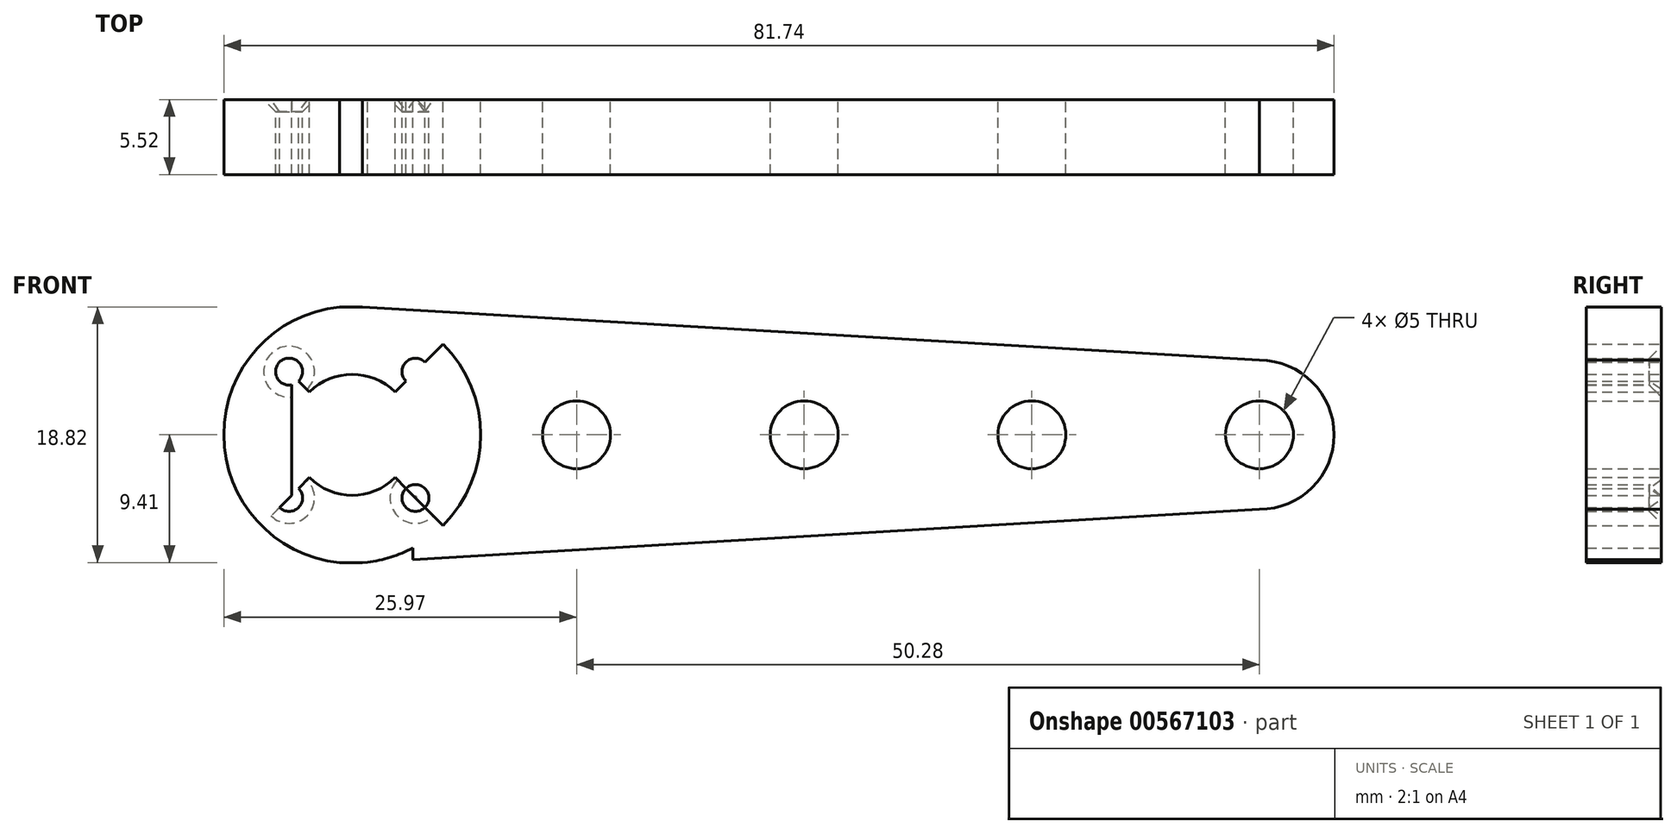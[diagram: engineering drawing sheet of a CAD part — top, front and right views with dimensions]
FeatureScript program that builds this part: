
annotation { "Feature Type Name" : "Feature", "Feature Type Description" : "" }
export const myFeature = defineFeature(function(context is Context, id is Id, definition is map)
    precondition{}
    {
        {
            var Q0;
            Q0=qCreatedBy(makeId("Front.planeOp"),FACE);
            var sketch = newSketch(context, id + "F0", { "sketchPlane" : qUnion([Q0])});
            skLineSegment(sketch, "E0.bottom", {"start": v(40.87, 9.41) * mm, "end": v(-40.87, 9.41) * mm});
            skLineSegment(sketch, "E0.top", {"start": v(40.87, -9.4) * mm, "end": v(-40.87, -9.4) * mm});
            skLineSegment(sketch, "E0.left", {"start": v(40.87, 9.41) * mm, "end": v(40.87, -9.4) * mm});
            skLineSegment(sketch, "E0.right", {"start": v(-40.87, 9.41) * mm, "end": v(-40.87, -9.4) * mm});
            skPoint(sketch, "E0.middle", {"position": v(0, 0) * mm});
            skLineSegment(sketch, "E1", {"start": v(-35.87, 9.41) * mm, "end": v(-35.87, -9.4) * mm});
            skLineSegment(sketch, "E2", {"start": v(-26.96, 9.41) * mm, "end": v(-26.96, -9.4) * mm});
            skLineSegment(sketch, "E3", {"start": v(-35.87, 0) * mm, "end": v(-26.96, 0) * mm});
            skCircle(sketch, "E4", {"center": v(-31.41, 0) * mm, "radius": 4.46 * mm});
            skLineSegment(sketch, "E5", {"start": v(32.88, 9.4) * mm, "end": v(32.88, -9.4) * mm});
            skLineSegment(sketch, "E6", {"start": v(37.88, 9.4) * mm, "end": v(37.88, -9.4) * mm});
            skLineSegment(sketch, "E7", {"start": v(37.88, 0) * mm, "end": v(32.88, 0) * mm});
            skCircle(sketch, "E8", {"center": v(35.38, 0) * mm, "radius": 2.5 * mm});
            skLineSegment(sketch, "E9", {"start": v(21.12, 9.4) * mm, "end": v(21.12, -9.4) * mm});
            skLineSegment(sketch, "E10", {"start": v(16.12, 9.4) * mm, "end": v(16.12, -9.4) * mm});
            skLineSegment(sketch, "E11", {"start": v(4.36, 9.4) * mm, "end": v(4.36, -9.4) * mm});
            skLineSegment(sketch, "E12", {"start": v(-0.64, 9.4) * mm, "end": v(-0.64, -9.4) * mm});
            skLineSegment(sketch, "E13", {"start": v(-12.4, 9.4) * mm, "end": v(-12.4, -9.4) * mm});
            skLineSegment(sketch, "E14", {"start": v(-17.4, 9.4) * mm, "end": v(-17.4, -9.4) * mm});
            skLineSegment(sketch, "E15", {"start": v(-17.4, 0) * mm, "end": v(-12.4, 0) * mm});
            skLineSegment(sketch, "E16", {"start": v(-0.64, 0) * mm, "end": v(4.36, 0) * mm});
            skLineSegment(sketch, "E17", {"start": v(16.12, 0) * mm, "end": v(21.12, 0) * mm});
            skCircle(sketch, "E18", {"center": v(-14.9, 0) * mm, "radius": 2.5 * mm});
            skCircle(sketch, "E19", {"center": v(1.86, 0) * mm, "radius": 2.5 * mm});
            skCircle(sketch, "E20", {"center": v(18.62, 0) * mm, "radius": 2.5 * mm});
            skLineSegment(sketch, "E21", {"start": v(-31.41, 0) * mm, "end": v(-40.67, 9.25) * mm});
            skLineSegment(sketch, "E22", {"start": v(-31.41, 0) * mm, "end": v(-22.16, 9.25) * mm});
            skLineSegment(sketch, "E23", {"start": v(-31.41, 0) * mm, "end": v(-22.16, -9.25) * mm});
            skLineSegment(sketch, "E24", {"start": v(-31.41, 0) * mm, "end": v(-40.67, -9.25) * mm});
            skLineSegment(sketch, "E25", {"start": v(-28.26, 3.15) * mm, "end": v(-28.26, -3.15) * mm});
            skLineSegment(sketch, "E26", {"start": v(-28.26, -3.15) * mm, "end": v(-34.57, -3.15) * mm});
            skLineSegment(sketch, "E27", {"start": v(-34.57, -3.15) * mm, "end": v(-34.57, 3.15) * mm});
            skLineSegment(sketch, "E28", {"start": v(-34.57, 3.15) * mm, "end": v(-28.26, 3.15) * mm});
            skLineSegment(sketch, "E29", {"start": v(-28.26, 3.15) * mm, "end": v(-27.47, 3.95) * mm});
            skLineSegment(sketch, "E30", {"start": v(-27.47, 3.95) * mm, "end": v(-26.06, 5.35) * mm});
            skCircle(sketch, "E31", {"center": v(-26.76, 4.65) * mm, "radius": 1 * mm});
            skCircle(sketch, "E32.MirrorC", {"center": v(-26.76, -4.65) * mm, "radius": 1 * mm});
            skCircle(sketch, "E33.MirrorC", {"center": v(-36.07, -4.65) * mm, "radius": 1 * mm});
            skCircle(sketch, "E34.MirrorC", {"center": v(-36.07, 4.65) * mm, "radius": 1 * mm});
            skCircle(sketch, "E35", {"center": v(-31.41, 0) * mm, "radius": 9.46 * mm});
            skCircle(sketch, "E36", {"center": v(35.38, 0) * mm, "radius": 5.49 * mm});
            skLineSegment(sketch, "E37", {"start": v(35.38, 0) * mm, "end": v(35.38, 5.49) * mm});
            skLineSegment(sketch, "E38", {"start": v(35.38, 0) * mm, "end": v(35.38, -5.49) * mm});
            skLineSegment(sketch, "E39", {"start": v(-31.41, 0) * mm, "end": v(-31.41, -9.46) * mm});
            skLineSegment(sketch, "E40", {"start": v(-31.41, 0) * mm, "end": v(-31.41, 9.46) * mm});
            skLineSegment(sketch, "E41", {"start": v(-31.41, 9.46) * mm, "end": v(35.38, 5.49) * mm});
            skLineSegment(sketch, "E42", {"start": v(35.38, -5.49) * mm, "end": v(-31.41, -9.46) * mm});
            skSolve(sketch);
        }
        {
            var Q0;
            {var subQ5=sQuery(id+"F0.wireOp",EDGE,"E35");var subQ11=sQuery(id+"F0.wireOp",EDGE,"E0.bottom");var subQ12=makeQuery(id+"F0.imprint","INTERSECT",VERTEX,{"disambiguationData":[OD(1.0)],"derivedFrom":[subQ11,subQ5]});Q0=makeQuery(id+"F0.imprint","IMPRINT",FACE,{"disambiguationData":[TD([[makeQuery(id+"F0.imprint","IMPRINT",EDGE,{"disambiguationData":[TD([[subQ12,1.0]])],"derivedFrom":subQ11}),1.0]])]});}
            var Q1;
            {var subQ0=sQuery(id+"F0.wireOp",EDGE,"E35");var subQ5=sQuery(id+"F0.wireOp",EDGE,"E21");var subQ6=makeQuery(id+"F0.imprint","INTERSECT",VERTEX,{"derivedFrom":[subQ5,subQ0]});Q1=makeQuery(id+"F0.imprint","IMPRINT",FACE,{"disambiguationData":[TD([[makeQuery(id+"F0.imprint","IMPRINT",EDGE,{"disambiguationData":[TD([[subQ6,1.0]])],"derivedFrom":subQ5}),1.0]])]});}
            var Q2;
            {var subQ0=sQuery(id+"F0.wireOp",EDGE,"E35");var subQ1=sQuery(id+"F0.wireOp",EDGE,"E1");var subQ2=makeQuery(id+"F0.imprint","INTERSECT",VERTEX,{"disambiguationData":[OD(0.0)],"derivedFrom":[subQ1,subQ0]});Q2=makeQuery(id+"F0.imprint","IMPRINT",FACE,{"disambiguationData":[TD([[makeQuery(id+"F0.imprint","IMPRINT",EDGE,{"disambiguationData":[TD([[subQ2,-1.0]])],"derivedFrom":subQ1}),-1.0]])]});}
            var Q3;
            {var subQ1=sQuery(id+"F0.wireOp",EDGE,"E1");var subQ3=sQuery(id+"F0.wireOp",EDGE,"E34.MirrorC");var subQ4=makeQuery(id+"F0.imprint","INTERSECT",VERTEX,{"disambiguationData":[OD(1.0)],"derivedFrom":[subQ1,subQ3]});Q3=makeQuery(id+"F0.imprint","IMPRINT",FACE,{"disambiguationData":[TD([[makeQuery(id+"F0.imprint","IMPRINT",EDGE,{"disambiguationData":[TD([[subQ4,-1.0]])],"derivedFrom":subQ3}),-1.0]])]});}
            var Q4;
            {var subQ0=sQuery(id+"F0.wireOp",EDGE,"E33.MirrorC");var subQ1=sQuery(id+"F0.wireOp",EDGE,"E1");var subQ2=makeQuery(id+"F0.imprint","INTERSECT",VERTEX,{"disambiguationData":[OD(1.0)],"derivedFrom":[subQ1,subQ0]});Q4=makeQuery(id+"F0.imprint","IMPRINT",FACE,{"disambiguationData":[TD([[makeQuery(id+"F0.imprint","IMPRINT",EDGE,{"disambiguationData":[TD([[subQ2,-1.0]])],"derivedFrom":subQ1}),-1.0]])]});}
            var Q5;
            {var subQ9=sQuery(id+"F0.wireOp",EDGE,"E35");var subQ11=sQuery(id+"F0.wireOp",EDGE,"E0.top");var subQ12=makeQuery(id+"F0.imprint","INTERSECT",VERTEX,{"disambiguationData":[OD(1.0)],"derivedFrom":[subQ11,subQ9]});Q5=makeQuery(id+"F0.imprint","IMPRINT",FACE,{"disambiguationData":[TD([[makeQuery(id+"F0.imprint","IMPRINT",EDGE,{"disambiguationData":[TD([[subQ12,1.0]])],"derivedFrom":subQ11}),-1.0]])]});}
            var Q6;
            {var subQ1=sQuery(id+"F0.wireOp",EDGE,"E1");var subQ3=sQuery(id+"F0.wireOp",EDGE,"E33.MirrorC");var subQ4=makeQuery(id+"F0.imprint","INTERSECT",VERTEX,{"disambiguationData":[OD(0.0)],"derivedFrom":[subQ1,subQ3]});Q6=makeQuery(id+"F0.imprint","IMPRINT",FACE,{"disambiguationData":[TD([[makeQuery(id+"F0.imprint","IMPRINT",EDGE,{"disambiguationData":[TD([[subQ4,-1.0]])],"derivedFrom":subQ3}),1.0]])]});}
            var Q7;
            {var subQ11=sQuery(id+"F0.wireOp",EDGE,"E42");var subQ12=sQuery(id+"F0.wireOp",EDGE,"E0.top");var subQ13=makeQuery(id+"F0.imprint","INTERSECT",VERTEX,{"derivedFrom":[subQ12,subQ11]});Q7=makeQuery(id+"F0.imprint","IMPRINT",FACE,{"disambiguationData":[TD([[makeQuery(id+"F0.imprint","IMPRINT",EDGE,{"disambiguationData":[TD([[subQ13,-1.0]])],"derivedFrom":subQ12}),-1.0]])]});}
            var Q8;
            {var subQ0=sQuery(id+"F0.wireOp",EDGE,"E32.MirrorC");var subQ1=sQuery(id+"F0.wireOp",EDGE,"E2");var subQ2=makeQuery(id+"F0.imprint","INTERSECT",VERTEX,{"disambiguationData":[OD(1.0)],"derivedFrom":[subQ1,subQ0]});Q8=makeQuery(id+"F0.imprint","IMPRINT",FACE,{"disambiguationData":[TD([[makeQuery(id+"F0.imprint","IMPRINT",EDGE,{"disambiguationData":[TD([[subQ2,-1.0]])],"derivedFrom":subQ1}),1.0]])]});}
            var Q9;
            {var subQ7=sQuery(id+"F0.wireOp",EDGE,"E32.MirrorC");var subQ9=sQuery(id+"F0.wireOp",EDGE,"E23");var subQ10=makeQuery(id+"F0.imprint","INTERSECT",VERTEX,{"disambiguationData":[OD(1.0)],"derivedFrom":[subQ9,subQ7]});Q9=makeQuery(id+"F0.imprint","IMPRINT",FACE,{"disambiguationData":[TD([[makeQuery(id+"F0.imprint","IMPRINT",EDGE,{"disambiguationData":[TD([[subQ10,-1.0]])],"derivedFrom":subQ9}),1.0]])]});}
            var Q10;
            {var subQ1=sQuery(id+"F0.wireOp",EDGE,"E2");var subQ3=sQuery(id+"F0.wireOp",EDGE,"E32.MirrorC");var subQ4=makeQuery(id+"F0.imprint","INTERSECT",VERTEX,{"disambiguationData":[OD(0.0)],"derivedFrom":[subQ1,subQ3]});Q10=makeQuery(id+"F0.imprint","IMPRINT",FACE,{"disambiguationData":[TD([[makeQuery(id+"F0.imprint","IMPRINT",EDGE,{"disambiguationData":[TD([[subQ4,1.0]])],"derivedFrom":subQ3}),1.0]])]});}
            var Q11;
            {var subQ0=sQuery(id+"F0.wireOp",EDGE,"E29");Q11=makeQuery(id+"F0.imprint","IMPRINT",FACE,{"disambiguationData":[TD([[makeQuery(id+"F0.imprint","IMPRINT",EDGE,{"derivedFrom":subQ0}),1.0]])]});}
            var Q12;
            {var subQ0=sQuery(id+"F0.wireOp",EDGE,"E35");var subQ1=sQuery(id+"F0.wireOp",EDGE,"E2");var subQ2=makeQuery(id+"F0.imprint","INTERSECT",VERTEX,{"disambiguationData":[OD(0.0)],"derivedFrom":[subQ1,subQ0]});Q12=makeQuery(id+"F0.imprint","IMPRINT",FACE,{"disambiguationData":[TD([[makeQuery(id+"F0.imprint","IMPRINT",EDGE,{"disambiguationData":[TD([[subQ2,-1.0]])],"derivedFrom":subQ1}),1.0]])]});}
            var Q13;
            {var subQ5=sQuery(id+"F0.wireOp",EDGE,"E29");Q13=makeQuery(id+"F0.imprint","IMPRINT",FACE,{"disambiguationData":[TD([[makeQuery(id+"F0.imprint","IMPRINT",EDGE,{"derivedFrom":subQ5}),-1.0]])]});}
            var Q14;
            {var subQ0=sQuery(id+"F0.wireOp",EDGE,"E41");var subQ1=sQuery(id+"F0.wireOp",EDGE,"E22");var subQ2=makeQuery(id+"F0.imprint","INTERSECT",VERTEX,{"derivedFrom":[subQ1,subQ0]});Q14=makeQuery(id+"F0.imprint","IMPRINT",FACE,{"disambiguationData":[TD([[makeQuery(id+"F0.imprint","IMPRINT",EDGE,{"disambiguationData":[TD([[subQ2,1.0]])],"derivedFrom":subQ1}),-1.0]])]});}
            var Q15;
            {var subQ0=sQuery(id+"F0.wireOp",EDGE,"E41");var subQ1=sQuery(id+"F0.wireOp",EDGE,"E2");var subQ2=makeQuery(id+"F0.imprint","INTERSECT",VERTEX,{"derivedFrom":[subQ1,subQ0]});Q15=makeQuery(id+"F0.imprint","IMPRINT",FACE,{"disambiguationData":[TD([[makeQuery(id+"F0.imprint","IMPRINT",EDGE,{"disambiguationData":[TD([[subQ2,-1.0]])],"derivedFrom":subQ1}),1.0]])]});}
            var Q16;
            {var subQ0=sQuery(id+"F0.wireOp",EDGE,"E41");var subQ1=sQuery(id+"F0.wireOp",EDGE,"E2");var subQ2=makeQuery(id+"F0.imprint","INTERSECT",VERTEX,{"derivedFrom":[subQ1,subQ0]});Q16=makeQuery(id+"F0.imprint","IMPRINT",FACE,{"disambiguationData":[TD([[makeQuery(id+"F0.imprint","IMPRINT",EDGE,{"disambiguationData":[TD([[subQ2,-1.0]])],"derivedFrom":subQ1}),-1.0]])]});}
            var Q17;
            {var subQ0=sQuery(id+"F0.wireOp",EDGE,"E35");var subQ1=sQuery(id+"F0.wireOp",EDGE,"E2");var subQ2=makeQuery(id+"F0.imprint","INTERSECT",VERTEX,{"disambiguationData":[OD(1.0)],"derivedFrom":[subQ1,subQ0]});Q17=makeQuery(id+"F0.imprint","IMPRINT",FACE,{"disambiguationData":[TD([[makeQuery(id+"F0.imprint","IMPRINT",EDGE,{"disambiguationData":[TD([[subQ2,-1.0]])],"derivedFrom":subQ1}),1.0]])]});}
            var Q18;
            {var subQ0=sQuery(id+"F0.wireOp",EDGE,"E35");var subQ1=sQuery(id+"F0.wireOp",EDGE,"E2");var subQ2=makeQuery(id+"F0.imprint","INTERSECT",VERTEX,{"disambiguationData":[OD(1.0)],"derivedFrom":[subQ1,subQ0]});Q18=makeQuery(id+"F0.imprint","IMPRINT",FACE,{"disambiguationData":[TD([[makeQuery(id+"F0.imprint","IMPRINT",EDGE,{"disambiguationData":[TD([[subQ2,-1.0]])],"derivedFrom":subQ1}),-1.0]])]});}
            var Q19;
            {var subQ2=sQuery(id+"F0.wireOp",EDGE,"E13");var subQ4=sQuery(id+"F0.wireOp",EDGE,"E42");var subQ5=makeQuery(id+"F0.imprint","INTERSECT",VERTEX,{"derivedFrom":[subQ2,subQ4]});Q19=makeQuery(id+"F0.imprint","IMPRINT",FACE,{"disambiguationData":[TD([[makeQuery(id+"F0.imprint","IMPRINT",EDGE,{"disambiguationData":[TD([[subQ5,-1.0]])],"derivedFrom":subQ4}),-1.0]])]});}
            var Q20;
            {var subQ2=sQuery(id+"F0.wireOp",EDGE,"E13");var subQ4=sQuery(id+"F0.wireOp",EDGE,"E41");var subQ5=makeQuery(id+"F0.imprint","INTERSECT",VERTEX,{"derivedFrom":[subQ2,subQ4]});Q20=makeQuery(id+"F0.imprint","IMPRINT",FACE,{"disambiguationData":[TD([[makeQuery(id+"F0.imprint","IMPRINT",EDGE,{"disambiguationData":[TD([[subQ5,1.0]])],"derivedFrom":subQ4}),-1.0]])]});}
            var Q21;
            {var subQ2=sQuery(id+"F0.wireOp",EDGE,"E41");var subQ4=sQuery(id+"F0.wireOp",EDGE,"E12");var subQ9=makeQuery(id+"F0.imprint","INTERSECT",VERTEX,{"derivedFrom":[subQ4,subQ2]});Q21=makeQuery(id+"F0.imprint","IMPRINT",FACE,{"disambiguationData":[TD([[makeQuery(id+"F0.imprint","IMPRINT",EDGE,{"disambiguationData":[TD([[subQ9,1.0]])],"derivedFrom":subQ2}),-1.0]])]});}
            var Q22;
            {var subQ2=sQuery(id+"F0.wireOp",EDGE,"E41");var subQ5=sQuery(id+"F0.wireOp",EDGE,"E10");var subQ9=makeQuery(id+"F0.imprint","INTERSECT",VERTEX,{"derivedFrom":[subQ5,subQ2]});Q22=makeQuery(id+"F0.imprint","IMPRINT",FACE,{"disambiguationData":[TD([[makeQuery(id+"F0.imprint","IMPRINT",EDGE,{"disambiguationData":[TD([[subQ9,1.0]])],"derivedFrom":subQ2}),-1.0]])]});}
            var Q23;
            {var subQ2=sQuery(id+"F0.wireOp",EDGE,"E11");var subQ4=sQuery(id+"F0.wireOp",EDGE,"E42");var subQ5=makeQuery(id+"F0.imprint","INTERSECT",VERTEX,{"derivedFrom":[subQ2,subQ4]});Q23=makeQuery(id+"F0.imprint","IMPRINT",FACE,{"disambiguationData":[TD([[makeQuery(id+"F0.imprint","IMPRINT",EDGE,{"disambiguationData":[TD([[subQ5,-1.0]])],"derivedFrom":subQ4}),-1.0]])]});}
            var Q24;
            {var subQ2=sQuery(id+"F0.wireOp",EDGE,"E11");var subQ4=sQuery(id+"F0.wireOp",EDGE,"E41");var subQ5=makeQuery(id+"F0.imprint","INTERSECT",VERTEX,{"derivedFrom":[subQ2,subQ4]});Q24=makeQuery(id+"F0.imprint","IMPRINT",FACE,{"disambiguationData":[TD([[makeQuery(id+"F0.imprint","IMPRINT",EDGE,{"disambiguationData":[TD([[subQ5,1.0]])],"derivedFrom":subQ4}),-1.0]])]});}
            var Q25;
            {var subQ2=sQuery(id+"F0.wireOp",EDGE,"E9");var subQ4=sQuery(id+"F0.wireOp",EDGE,"E41");var subQ5=makeQuery(id+"F0.imprint","INTERSECT",VERTEX,{"derivedFrom":[subQ2,subQ4]});Q25=makeQuery(id+"F0.imprint","IMPRINT",FACE,{"disambiguationData":[TD([[makeQuery(id+"F0.imprint","IMPRINT",EDGE,{"disambiguationData":[TD([[subQ5,1.0]])],"derivedFrom":subQ4}),-1.0]])]});}
            var Q26;
            {var subQ2=sQuery(id+"F0.wireOp",EDGE,"E9");var subQ4=sQuery(id+"F0.wireOp",EDGE,"E42");var subQ5=makeQuery(id+"F0.imprint","INTERSECT",VERTEX,{"derivedFrom":[subQ2,subQ4]});Q26=makeQuery(id+"F0.imprint","IMPRINT",FACE,{"disambiguationData":[TD([[makeQuery(id+"F0.imprint","IMPRINT",EDGE,{"disambiguationData":[TD([[subQ5,-1.0]])],"derivedFrom":subQ4}),-1.0]])]});}
            var Q27;
            {var subQ4=sQuery(id+"F0.wireOp",EDGE,"E41");var subQ7=sQuery(id+"F0.wireOp",EDGE,"E5");var subQ10=makeQuery(id+"F0.imprint","INTERSECT",VERTEX,{"derivedFrom":[subQ7,subQ4]});Q27=makeQuery(id+"F0.imprint","IMPRINT",FACE,{"disambiguationData":[TD([[makeQuery(id+"F0.imprint","IMPRINT",EDGE,{"disambiguationData":[TD([[subQ10,-1.0]])],"derivedFrom":subQ7}),-1.0]])]});}
            var Q28;
            {var subQ0=sQuery(id+"F0.wireOp",EDGE,"E5");var subQ2=sQuery(id+"F0.wireOp",EDGE,"E36");var subQ3=makeQuery(id+"F0.imprint","INTERSECT",VERTEX,{"disambiguationData":[OD(0.0)],"derivedFrom":[subQ0,subQ2]});Q28=makeQuery(id+"F0.imprint","IMPRINT",FACE,{"disambiguationData":[TD([[makeQuery(id+"F0.imprint","IMPRINT",EDGE,{"disambiguationData":[TD([[subQ3,-1.0]])],"derivedFrom":subQ2}),1.0]])]});}
            var Q29;
            {var subQ2=sQuery(id+"F0.wireOp",EDGE,"E36");var subQ4=makeQuery(id+"F0.imprint","INTERSECT",VERTEX,{"derivedFrom":[sQuery(id+"F0.wireOp",EDGE,"E0.left"),subQ2]});Q29=makeQuery(id+"F0.imprint","IMPRINT",FACE,{"disambiguationData":[TD([[makeQuery(id+"F0.imprint","IMPRINT",EDGE,{"disambiguationData":[TD([[subQ4,-1.0]])],"derivedFrom":subQ2}),1.0]])]});}
            var Q30;
            {var subQ1=sQuery(id+"F0.wireOp",EDGE,"E6");var subQ3=sQuery(id+"F0.wireOp",EDGE,"E36");var subQ4=makeQuery(id+"F0.imprint","INTERSECT",VERTEX,{"disambiguationData":[OD(0.0)],"derivedFrom":[subQ1,subQ3]});Q30=makeQuery(id+"F0.imprint","IMPRINT",FACE,{"disambiguationData":[TD([[makeQuery(id+"F0.imprint","IMPRINT",EDGE,{"disambiguationData":[TD([[subQ4,-1.0]])],"derivedFrom":subQ1}),-1.0]])]});}
            var Q31;
            {var subQ1=sQuery(id+"F0.wireOp",EDGE,"E6");var subQ3=sQuery(id+"F0.wireOp",EDGE,"E36");var subQ4=makeQuery(id+"F0.imprint","INTERSECT",VERTEX,{"disambiguationData":[OD(1.0)],"derivedFrom":[subQ1,subQ3]});Q31=makeQuery(id+"F0.imprint","IMPRINT",FACE,{"disambiguationData":[TD([[makeQuery(id+"F0.imprint","IMPRINT",EDGE,{"disambiguationData":[TD([[subQ4,1.0]])],"derivedFrom":subQ1}),-1.0]])]});}
            var Q32;
            {var subQ1=sQuery(id+"F0.wireOp",EDGE,"E5");var subQ3=sQuery(id+"F0.wireOp",EDGE,"E36");var subQ4=makeQuery(id+"F0.imprint","INTERSECT",VERTEX,{"disambiguationData":[OD(1.0)],"derivedFrom":[subQ1,subQ3]});Q32=makeQuery(id+"F0.imprint","IMPRINT",FACE,{"disambiguationData":[TD([[makeQuery(id+"F0.imprint","IMPRINT",EDGE,{"disambiguationData":[TD([[subQ4,1.0]])],"derivedFrom":subQ1}),1.0]])]});}
            var Q33;
            {var subQ1=sQuery(id+"F0.wireOp",EDGE,"E5");var subQ3=sQuery(id+"F0.wireOp",EDGE,"E36");var subQ4=makeQuery(id+"F0.imprint","INTERSECT",VERTEX,{"disambiguationData":[OD(0.0)],"derivedFrom":[subQ1,subQ3]});Q33=makeQuery(id+"F0.imprint","IMPRINT",FACE,{"disambiguationData":[TD([[makeQuery(id+"F0.imprint","IMPRINT",EDGE,{"disambiguationData":[TD([[subQ4,-1.0]])],"derivedFrom":subQ1}),1.0]])]});}
            var Q34;
            {var subQ0=sQuery(id+"F0.wireOp",EDGE,"E36");var subQ1=sQuery(id+"F0.wireOp",EDGE,"E5");var subQ2=makeQuery(id+"F0.imprint","INTERSECT",VERTEX,{"disambiguationData":[OD(1.0)],"derivedFrom":[subQ1,subQ0]});Q34=makeQuery(id+"F0.imprint","IMPRINT",FACE,{"disambiguationData":[TD([[makeQuery(id+"F0.imprint","IMPRINT",EDGE,{"disambiguationData":[TD([[subQ2,-1.0]])],"derivedFrom":subQ1}),1.0]])]});}
            var Q35;
            {var subQ0=sQuery(id+"F0.wireOp",EDGE,"E41");var subQ1=sQuery(id+"F0.wireOp",EDGE,"E5");var subQ2=makeQuery(id+"F0.imprint","INTERSECT",VERTEX,{"derivedFrom":[subQ1,subQ0]});Q35=makeQuery(id+"F0.imprint","IMPRINT",FACE,{"disambiguationData":[TD([[makeQuery(id+"F0.imprint","IMPRINT",EDGE,{"disambiguationData":[TD([[subQ2,-1.0]])],"derivedFrom":subQ1}),1.0]])]});}
            extrude(context, id + "F1", {"entities" : qUnion([Q0, Q1, Q2, Q3, Q4, Q5, Q6, Q7, Q8, Q9, Q10, Q11, Q12, Q13, Q14, Q15, Q16, Q17, Q18, Q19, Q20, Q21, Q22, Q23, Q24, Q25, Q26, Q27, Q28, Q29, Q30, Q31, Q32, Q33, Q34, Q35]), "endBound" : BoundingType.SYMMETRIC, "depth" : 5.52 * mm, "offsetDistance" : 25 * mm});
        }
        {
            var Q0;
            Q0=makeQuery(id+"F1.opExtrude","CAP_EDGE",EDGE,{"disambiguationData":[OSD([sQuery(id+"F0.wireOp",EDGE,"E34.MirrorC")])],"isStart":true});
            var Q1;
            Q1=makeQuery(id+"F1.opExtrude","CAP_EDGE",EDGE,{"disambiguationData":[OSD([sQuery(id+"F0.wireOp",EDGE,"E31")])],"isStart":true});
            var Q2;
            Q2=makeQuery(id+"F1.opExtrude","CAP_EDGE",EDGE,{"disambiguationData":[OSD([sQuery(id+"F0.wireOp",EDGE,"E32.MirrorC")])],"isStart":true});
            var Q3;
            Q3=makeQuery(id+"F1.opExtrude","CAP_EDGE",EDGE,{"disambiguationData":[OSD([sQuery(id+"F0.wireOp",EDGE,"E33.MirrorC")])],"isStart":true});
            chamfer(context, id + "F2", {"entities" : qUnion([Q0, Q1, Q2, Q3]), "chamferType" : ChamferType.OFFSET_ANGLE, "width" : 0.88 * mm, "oppositeDirection" : false, "angle" : 45 * degree});
        }
        {
            var Q0;
            Q0=makeQuery(id+"F1.opExtrude","SWEPT_BODY",BODY,{"disambiguationData":[OSD([sQuery(id+"F0.wireOp",EDGE,"E0.bottom"),sQuery(id+"F0.wireOp",EDGE,"E0.top"),sQuery(id+"F0.wireOp",EDGE,"E4"),sQuery(id+"F0.wireOp",EDGE,"E8"),sQuery(id+"F0.wireOp",EDGE,"E18"),sQuery(id+"F0.wireOp",EDGE,"E19"),sQuery(id+"F0.wireOp",EDGE,"E20"),sQuery(id+"F0.wireOp",EDGE,"E31"),sQuery(id+"F0.wireOp",EDGE,"E32.MirrorC"),sQuery(id+"F0.wireOp",EDGE,"E33.MirrorC"),sQuery(id+"F0.wireOp",EDGE,"E34.MirrorC"),sQuery(id+"F0.wireOp",EDGE,"E35"),sQuery(id+"F0.wireOp",EDGE,"E36"),sQuery(id+"F0.wireOp",EDGE,"E41"),sQuery(id+"F0.wireOp",EDGE,"E42")])]});
            var Q1;
            Q1=makeQuery(id+"F1.opExtrude","CAP_EDGE",EDGE,{"disambiguationData":[OSD([sQuery(id+"F0.wireOp",EDGE,"E41")])],"isStart":false});
            transform(context, id + "F3", {"entities" : qUnion([Q0]), "transformType" : TransformType.ROTATION, "transformAxis" : qUnion([Q1]), "angle" : 180 * degree, "makeCopy" : true});
        }
        {
            var Q0;
            Q0=makeQuery(id+"F3.opPattern","COPY",BODY,{"derivedFrom":makeQuery(id+"F1.opExtrude","SWEPT_BODY",BODY,{"disambiguationData":[OSD([sQuery(id+"F0.wireOp",EDGE,"E0.bottom"),sQuery(id+"F0.wireOp",EDGE,"E0.top"),sQuery(id+"F0.wireOp",EDGE,"E4"),sQuery(id+"F0.wireOp",EDGE,"E8"),sQuery(id+"F0.wireOp",EDGE,"E18"),sQuery(id+"F0.wireOp",EDGE,"E19"),sQuery(id+"F0.wireOp",EDGE,"E20"),sQuery(id+"F0.wireOp",EDGE,"E31"),sQuery(id+"F0.wireOp",EDGE,"E32.MirrorC"),sQuery(id+"F0.wireOp",EDGE,"E33.MirrorC"),sQuery(id+"F0.wireOp",EDGE,"E34.MirrorC"),sQuery(id+"F0.wireOp",EDGE,"E35"),sQuery(id+"F0.wireOp",EDGE,"E36"),sQuery(id+"F0.wireOp",EDGE,"E41"),sQuery(id+"F0.wireOp",EDGE,"E42")])]}),"instanceName":"1"});
            transform(context, id + "F4", {"entities" : qUnion([Q0]), "transformType" : TransformType.TRANSLATION_3D, "dx" : 0 * mm, "dy" : 5.1 * mm, "dz" : 3.7 * mm, "makeCopy" : false});
        }
        {
            var Q0;
            Q0=makeQuery(id+"F3.opPattern","COPY",BODY,{"derivedFrom":makeQuery(id+"F1.opExtrude","SWEPT_BODY",BODY,{"disambiguationData":[OSD([sQuery(id+"F0.wireOp",EDGE,"E0.bottom"),sQuery(id+"F0.wireOp",EDGE,"E0.top"),sQuery(id+"F0.wireOp",EDGE,"E4"),sQuery(id+"F0.wireOp",EDGE,"E8"),sQuery(id+"F0.wireOp",EDGE,"E18"),sQuery(id+"F0.wireOp",EDGE,"E19"),sQuery(id+"F0.wireOp",EDGE,"E20"),sQuery(id+"F0.wireOp",EDGE,"E31"),sQuery(id+"F0.wireOp",EDGE,"E32.MirrorC"),sQuery(id+"F0.wireOp",EDGE,"E33.MirrorC"),sQuery(id+"F0.wireOp",EDGE,"E34.MirrorC"),sQuery(id+"F0.wireOp",EDGE,"E35"),sQuery(id+"F0.wireOp",EDGE,"E36"),sQuery(id+"F0.wireOp",EDGE,"E41"),sQuery(id+"F0.wireOp",EDGE,"E42")])]}),"instanceName":"1"});
            deleteBodies(context, id + "F5", {"entities" : qUnion([Q0])});
        }
    });
